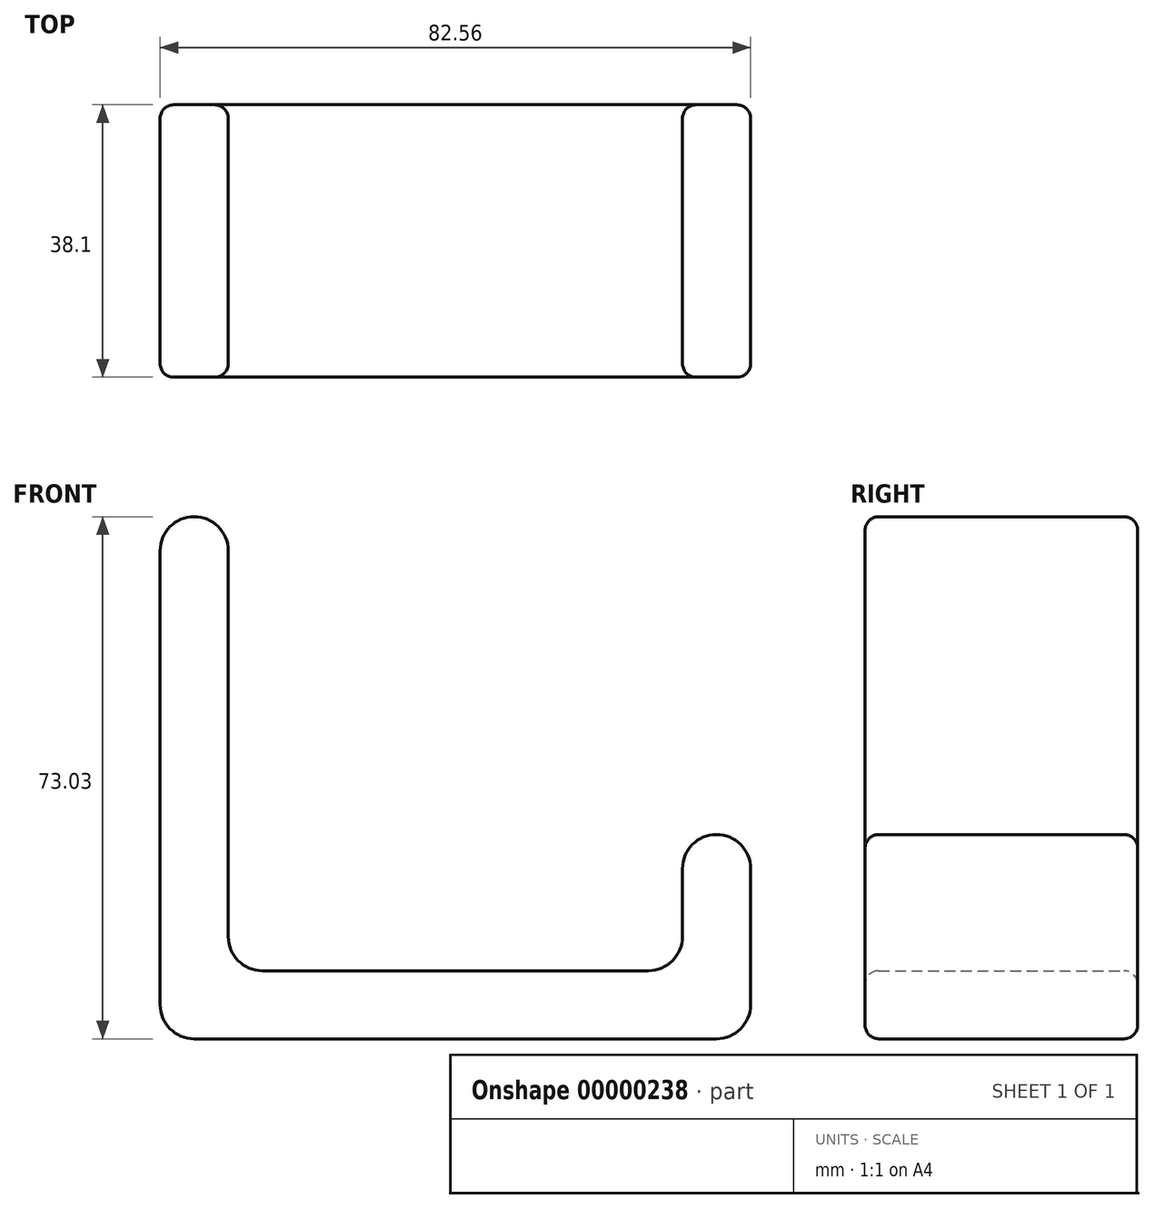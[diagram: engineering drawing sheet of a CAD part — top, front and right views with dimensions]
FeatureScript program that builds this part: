
annotation { "Feature Type Name" : "Feature", "Feature Type Description" : "" }
export const myFeature = defineFeature(function(context is Context, id is Id, definition is map)
    precondition{}
    {
        {
            var Q0;
            Q0=qCreatedBy(makeId("Front.planeOp"),FACE);
            var sketch = newSketch(context, id + "F0", { "sketchPlane" : qUnion([Q0])});
            skLineSegment(sketch, "E0", {"start": v(0, 31.75) * mm, "end": v(0, -31.75) * mm});
            skLineSegment(sketch, "E1", {"start": v(0, -31.75) * mm, "end": v(63.5, -31.75) * mm});
            skLineSegment(sketch, "E2", {"start": v(63.5, -31.75) * mm, "end": v(63.5, -12.7) * mm});
            skLineSegment(sketch, "E3.0", {"start": v(73.03, -41.27) * mm, "end": v(73.03, -12.7) * mm});
            skLineSegment(sketch, "E3.1", {"start": v(-9.52, -41.27) * mm, "end": v(73.03, -41.27) * mm});
            skLineSegment(sketch, "E3.2", {"start": v(-9.53, 31.75) * mm, "end": v(-9.52, -41.27) * mm});
            skLineSegment(sketch, "E4", {"start": v(-9.53, 31.75) * mm, "end": v(0, 31.75) * mm});
            skLineSegment(sketch, "E5", {"start": v(63.5, -12.7) * mm, "end": v(73.03, -12.7) * mm});
            skSolve(sketch);
        }
        {
            var Q0;
            Q0 = qSketchRegion(id + "F0", true);
            extrude(context, id + "F1", {"entities" : qUnion([Q0]), "depth" : 38.1 * mm, "symmetric" : true});
        }
        {
            var Q0;
            Q0=makeQuery(id+"F1.opExtrude","SWEPT_EDGE",EDGE,{"disambiguationData":[OSD([sQuery(id+"F0.wireOp",EDGE,"E0"),sQuery(id+"F0.wireOp",EDGE,"E1")])]});
            var Q1;
            Q1=makeQuery(id+"F1.opExtrude","SWEPT_EDGE",EDGE,{"disambiguationData":[OSD([sQuery(id+"F0.wireOp",EDGE,"E1"),sQuery(id+"F0.wireOp",EDGE,"E2")])]});
            var Q2;
            Q2=makeQuery(id+"F1.opExtrude","SWEPT_EDGE",EDGE,{"disambiguationData":[OSD([sQuery(id+"F0.wireOp",EDGE,"E2"),sQuery(id+"F0.wireOp",EDGE,"E5")])]});
            var Q3;
            Q3=makeQuery(id+"F1.opExtrude","SWEPT_EDGE",EDGE,{"disambiguationData":[OSD([sQuery(id+"F0.wireOp",EDGE,"E3.0"),sQuery(id+"F0.wireOp",EDGE,"E5")])]});
            var Q4;
            Q4=makeQuery(id+"F1.opExtrude","SWEPT_EDGE",EDGE,{"disambiguationData":[OSD([sQuery(id+"F0.wireOp",EDGE,"E3.0"),sQuery(id+"F0.wireOp",EDGE,"E3.1")])]});
            var Q5;
            Q5=makeQuery(id+"F1.opExtrude","SWEPT_EDGE",EDGE,{"disambiguationData":[OSD([sQuery(id+"F0.wireOp",EDGE,"E3.1"),sQuery(id+"F0.wireOp",EDGE,"E3.2")])]});
            var Q6;
            Q6=makeQuery(id+"F1.opExtrude","SWEPT_EDGE",EDGE,{"disambiguationData":[OSD([sQuery(id+"F0.wireOp",EDGE,"E3.2"),sQuery(id+"F0.wireOp",EDGE,"E4")])]});
            var Q7;
            Q7=makeQuery(id+"F1.opExtrude","SWEPT_EDGE",EDGE,{"disambiguationData":[OSD([sQuery(id+"F0.wireOp",EDGE,"E0"),sQuery(id+"F0.wireOp",EDGE,"E4")])]});
            fillet(context, id + "F2", {"entities" : qUnion([Q0, Q1, Q2, Q3, Q4, Q5, Q6, Q7]), "radius" : 4.76 * mm, "tangentPropagation" : true, "allowEdgeOverflow" : false});
        }
        {
            var Q0;
            Q0=makeQuery(id+"F1.opExtrude","CAP_EDGE",EDGE,{"disambiguationData":[OSD([sQuery(id+"F0.wireOp",EDGE,"E1")])],"isStart":false});
            var Q1;
            Q1=makeQuery(id+"F1.opExtrude","CAP_EDGE",EDGE,{"disambiguationData":[OSD([sQuery(id+"F0.wireOp",EDGE,"E1")])],"isStart":true});
            fillet(context, id + "F3", {"entities" : qUnion([Q0, Q1]), "radius" : 1.9 * mm, "tangentPropagation" : true, "allowEdgeOverflow" : false});
        }
    });
